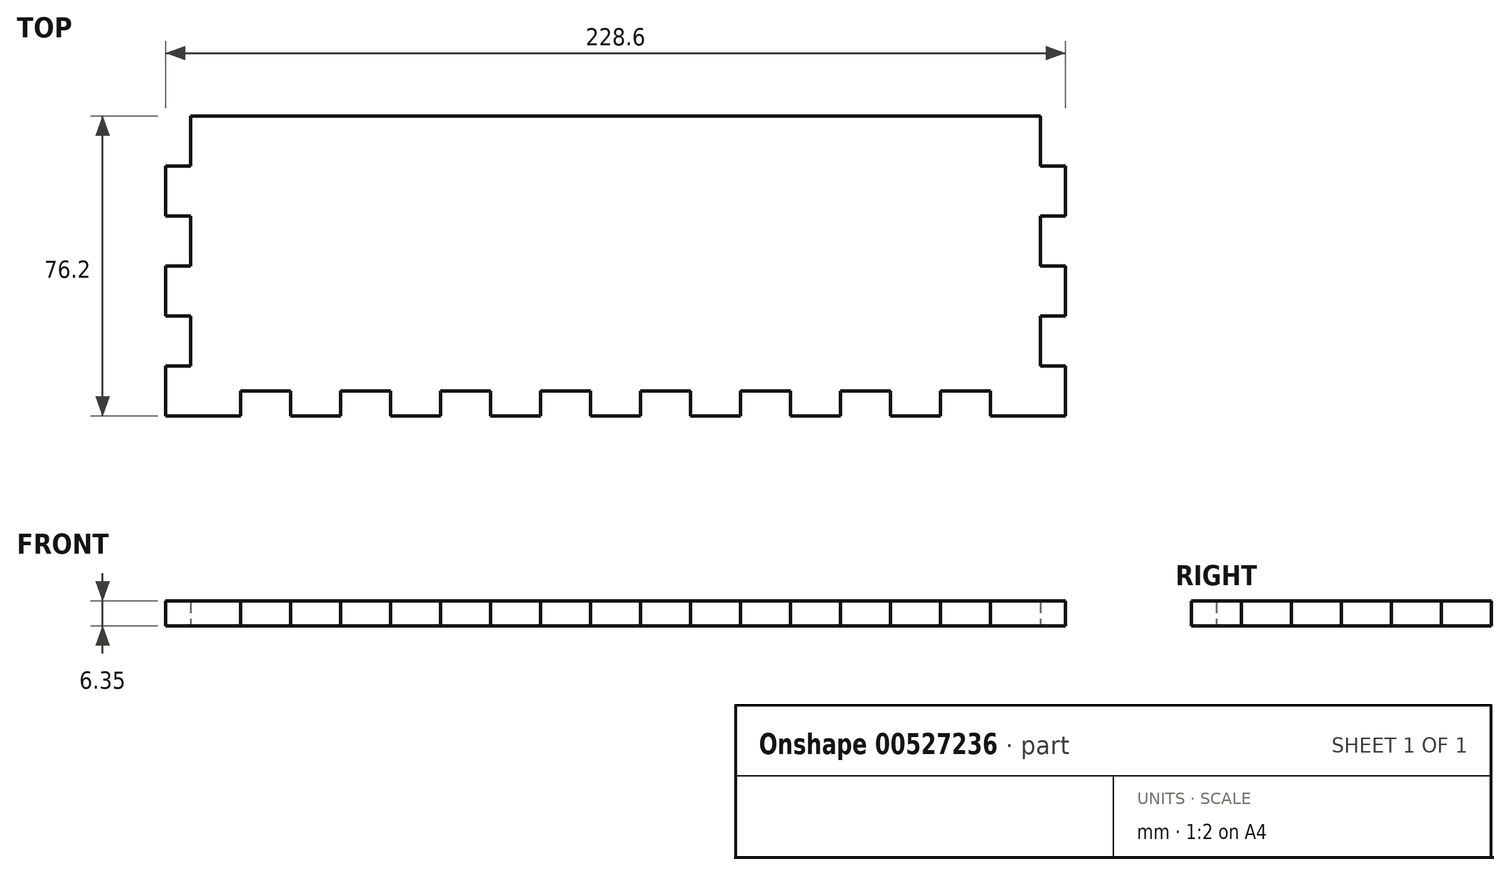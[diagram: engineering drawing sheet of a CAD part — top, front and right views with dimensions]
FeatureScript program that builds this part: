
annotation { "Feature Type Name" : "Feature", "Feature Type Description" : "" }
export const myFeature = defineFeature(function(context is Context, id is Id, definition is map)
    precondition{}
    {
        {
            var Q0;
            Q0=qCreatedBy(makeId("Top.planeOp"),FACE);
            var sketch = newSketch(context, id + "F0", { "sketchPlane" : qUnion([Q0])});
            skLineSegment(sketch, "E0.bottom", {"start": v(6.35, 0) * mm, "end": v(222.25, 0) * mm});
            skLineSegment(sketch, "E0.top", {"start": v(0, -76.2) * mm, "end": v(19.05, -76.2) * mm});
            skLineSegment(sketch, "E0.left", {"start": v(0, -12.7) * mm, "end": v(0, -25.4) * mm});
            skLineSegment(sketch, "E0.right", {"start": v(228.6, -12.7) * mm, "end": v(228.6, -25.4) * mm});
            skLineSegment(sketch, "E1", {"start": v(19.05, -76.2) * mm, "end": v(19.05, -69.85) * mm});
            skLineSegment(sketch, "E2", {"start": v(19.05, -69.85) * mm, "end": v(31.75, -69.85) * mm});
            skLineSegment(sketch, "E3", {"start": v(31.75, -69.85) * mm, "end": v(31.75, -76.2) * mm});
            skLineSegment(sketch, "E4", {"start": v(31.75, -76.2) * mm, "end": v(44.45, -76.2) * mm});
            skLineSegment(sketch, "E5", {"start": v(44.45, -76.2) * mm, "end": v(44.45, -69.85) * mm});
            skLineSegment(sketch, "E6", {"start": v(44.45, -69.85) * mm, "end": v(57.15, -69.85) * mm});
            skLineSegment(sketch, "E7", {"start": v(57.15, -69.85) * mm, "end": v(57.15, -76.2) * mm});
            skLineSegment(sketch, "E8", {"start": v(57.15, -76.2) * mm, "end": v(69.85, -76.2) * mm});
            skLineSegment(sketch, "E9", {"start": v(69.85, -76.2) * mm, "end": v(69.85, -69.85) * mm});
            skLineSegment(sketch, "E10", {"start": v(69.85, -69.85) * mm, "end": v(82.55, -69.85) * mm});
            skLineSegment(sketch, "E11", {"start": v(82.55, -69.85) * mm, "end": v(82.55, -76.2) * mm});
            skLineSegment(sketch, "E12", {"start": v(82.55, -76.2) * mm, "end": v(95.25, -76.2) * mm});
            skLineSegment(sketch, "E13", {"start": v(95.25, -76.2) * mm, "end": v(95.25, -69.85) * mm});
            skLineSegment(sketch, "E14", {"start": v(95.25, -69.85) * mm, "end": v(107.95, -69.85) * mm});
            skLineSegment(sketch, "E15", {"start": v(107.95, -69.85) * mm, "end": v(107.95, -76.2) * mm});
            skLineSegment(sketch, "E16.trimOffspring", {"start": v(107.95, -76.2) * mm, "end": v(120.65, -76.2) * mm});
            skLineSegment(sketch, "E17", {"start": v(120.65, -76.2) * mm, "end": v(120.65, -69.85) * mm});
            skLineSegment(sketch, "E18", {"start": v(120.65, -69.85) * mm, "end": v(133.35, -69.85) * mm});
            skLineSegment(sketch, "E19", {"start": v(133.35, -69.85) * mm, "end": v(133.35, -76.2) * mm});
            skLineSegment(sketch, "E20", {"start": v(133.35, -76.2) * mm, "end": v(146.05, -76.2) * mm});
            skLineSegment(sketch, "E21", {"start": v(146.05, -76.2) * mm, "end": v(146.05, -69.85) * mm});
            skLineSegment(sketch, "E22", {"start": v(146.05, -69.85) * mm, "end": v(158.75, -69.85) * mm});
            skLineSegment(sketch, "E23", {"start": v(158.75, -69.85) * mm, "end": v(158.75, -76.2) * mm});
            skLineSegment(sketch, "E24.trimOffspring", {"start": v(158.75, -76.2) * mm, "end": v(171.45, -76.2) * mm});
            skLineSegment(sketch, "E25", {"start": v(171.45, -76.2) * mm, "end": v(171.45, -69.85) * mm});
            skLineSegment(sketch, "E26", {"start": v(171.45, -69.85) * mm, "end": v(184.15, -69.85) * mm});
            skLineSegment(sketch, "E27", {"start": v(184.15, -69.85) * mm, "end": v(184.15, -76.2) * mm});
            skLineSegment(sketch, "E28", {"start": v(184.15, -76.2) * mm, "end": v(196.85, -76.2) * mm});
            skLineSegment(sketch, "E29", {"start": v(196.85, -76.2) * mm, "end": v(196.85, -69.85) * mm});
            skLineSegment(sketch, "E30", {"start": v(196.85, -69.85) * mm, "end": v(209.55, -69.85) * mm});
            skLineSegment(sketch, "E31", {"start": v(209.55, -69.85) * mm, "end": v(209.55, -76.2) * mm});
            skLineSegment(sketch, "E32.trimOffspring", {"start": v(209.55, -76.2) * mm, "end": v(228.6, -76.2) * mm});
            skLineSegment(sketch, "E33", {"start": v(0, -76.2) * mm, "end": v(0, -63.5) * mm});
            skLineSegment(sketch, "E34", {"start": v(0, -63.5) * mm, "end": v(6.35, -63.5) * mm});
            skLineSegment(sketch, "E35", {"start": v(6.35, -63.5) * mm, "end": v(6.35, -50.8) * mm});
            skLineSegment(sketch, "E36", {"start": v(6.35, -50.8) * mm, "end": v(0, -50.8) * mm});
            skLineSegment(sketch, "E37", {"start": v(0, -50.8) * mm, "end": v(0, -38.1) * mm});
            skLineSegment(sketch, "E38", {"start": v(0, -38.1) * mm, "end": v(6.35, -38.1) * mm});
            skLineSegment(sketch, "E39", {"start": v(6.35, -38.1) * mm, "end": v(6.35, -25.4) * mm});
            skLineSegment(sketch, "E40", {"start": v(6.35, -25.4) * mm, "end": v(0, -25.4) * mm});
            skLineSegment(sketch, "E41.trimOffspring", {"start": v(0, -38.1) * mm, "end": v(0, -50.8) * mm});
            skLineSegment(sketch, "E42.trimOffspring", {"start": v(0, -63.5) * mm, "end": v(0, -76.2) * mm});
            skLineSegment(sketch, "E43", {"start": v(0, -25.4) * mm, "end": v(0, -12.7) * mm});
            skLineSegment(sketch, "E44", {"start": v(0, -12.7) * mm, "end": v(6.35, -12.7) * mm});
            skLineSegment(sketch, "E45", {"start": v(6.35, -12.7) * mm, "end": v(6.35, 0) * mm});
            skPoint(sketch, "E46.orphan", {"position": v(0, 0) * mm});
            skLineSegment(sketch, "E47", {"start": v(114.3, -76.2) * mm, "end": v(114.3, -52.3) * mm, "construction": true});
            skLineSegment(sketch, "E48", {"start": v(228.6, -76.2) * mm, "end": v(228.6, -63.5) * mm});
            skLineSegment(sketch, "E49", {"start": v(228.6, -63.5) * mm, "end": v(222.25, -63.5) * mm});
            skLineSegment(sketch, "E50", {"start": v(222.25, -63.5) * mm, "end": v(222.25, -50.8) * mm});
            skLineSegment(sketch, "E51", {"start": v(222.25, -50.8) * mm, "end": v(228.6, -50.8) * mm});
            skLineSegment(sketch, "E52", {"start": v(228.6, -50.8) * mm, "end": v(228.6, -38.1) * mm});
            skLineSegment(sketch, "E53", {"start": v(228.6, -38.1) * mm, "end": v(222.25, -38.1) * mm});
            skLineSegment(sketch, "E54", {"start": v(222.25, -38.1) * mm, "end": v(222.25, -25.4) * mm});
            skLineSegment(sketch, "E55", {"start": v(222.25, -25.4) * mm, "end": v(228.6, -25.4) * mm});
            skLineSegment(sketch, "E56", {"start": v(228.6, -25.4) * mm, "end": v(228.6, -12.7) * mm});
            skLineSegment(sketch, "E57", {"start": v(228.6, -12.7) * mm, "end": v(222.25, -12.7) * mm});
            skLineSegment(sketch, "E58", {"start": v(222.25, -12.7) * mm, "end": v(222.25, 0) * mm});
            skPoint(sketch, "E59.orphan", {"position": v(228.6, 0) * mm});
            skLineSegment(sketch, "E60.trimOffspring", {"start": v(228.6, -38.1) * mm, "end": v(228.6, -50.8) * mm});
            skLineSegment(sketch, "E61.trimOffspring", {"start": v(228.6, -63.5) * mm, "end": v(228.6, -76.2) * mm});
            skSolve(sketch);
        }
        {
            var Q0;
            Q0=makeQuery(id+"F0.imprint","IMPRINT",FACE,{"disambiguationData":[TD([[makeQuery(id+"F0.imprint","IMPRINT",EDGE,{"derivedFrom":sQuery(id+"F0.wireOp",EDGE,"E0.bottom")}),-1.0]])]});
            extrude(context, id + "F1", {"entities" : qUnion([Q0]), "depth" : 6.35 * mm, "offsetDistance" : 25.4 * mm});
        }
    });
